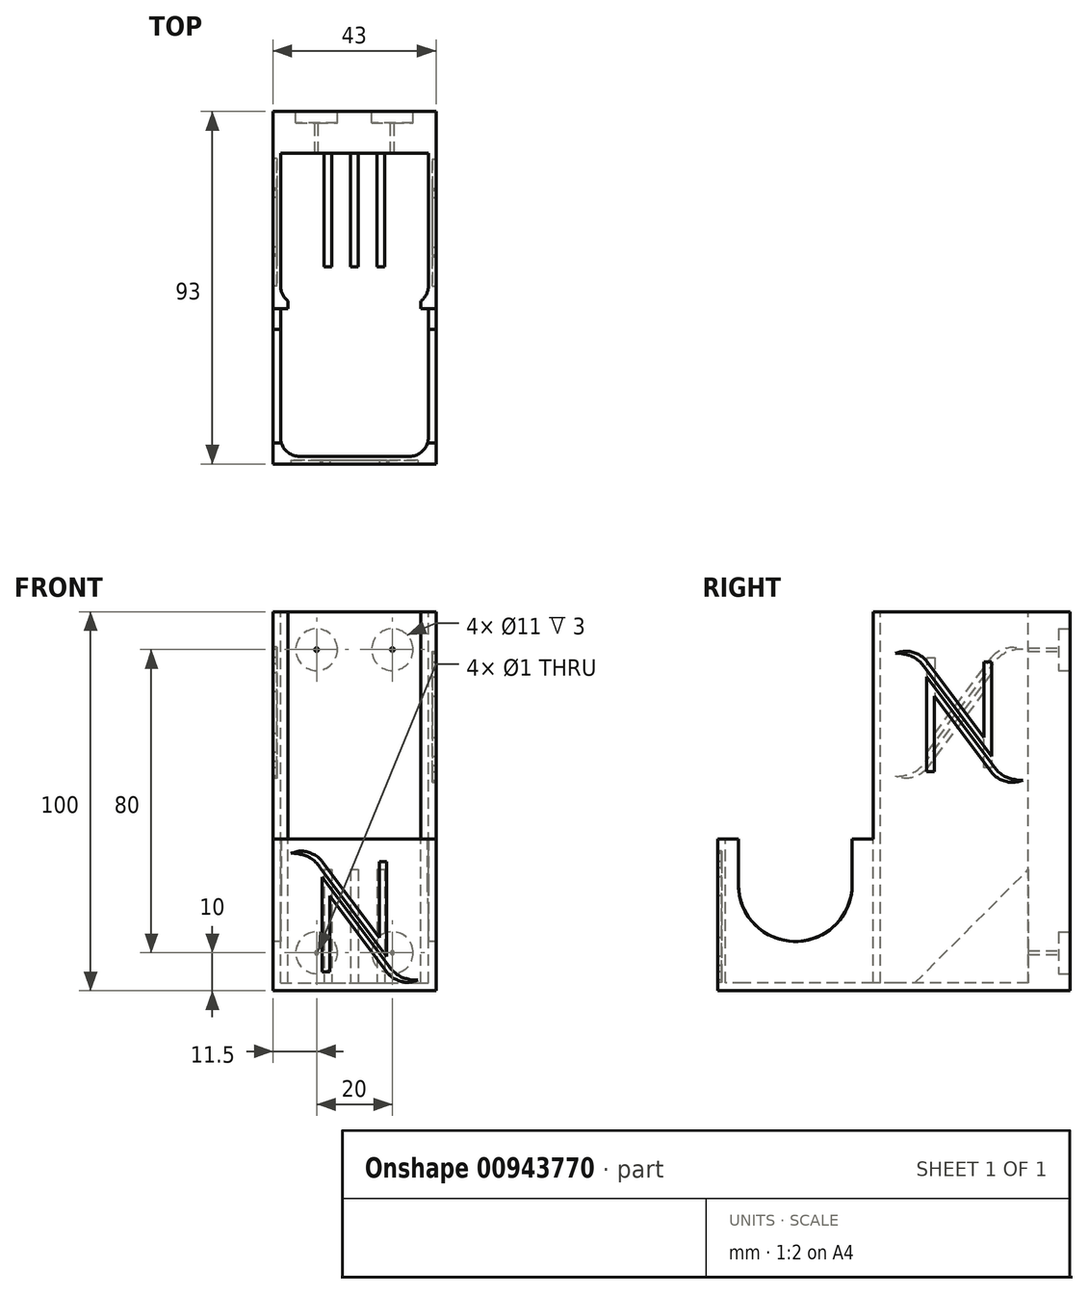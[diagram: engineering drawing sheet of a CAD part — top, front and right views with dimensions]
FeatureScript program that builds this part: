
annotation { "Feature Type Name" : "Feature", "Feature Type Description" : "" }
export const myFeature = defineFeature(function(context is Context, id is Id, definition is map)
    precondition{}
    {
        {
            var Q0;
            Q0=qCreatedBy(makeId("Top.planeOp"),FACE);
            var sketch = newSketch(context, id + "F0", { "sketchPlane" : qUnion([Q0])});
            skLineSegment(sketch, "E0.bottom", {"start": v(-21.5, 42) * mm, "end": v(21.5, 42) * mm});
            skLineSegment(sketch, "E0.top", {"start": v(-21.5, -42) * mm, "end": v(21.5, -42) * mm});
            skLineSegment(sketch, "E0.left", {"start": v(-21.5, 42) * mm, "end": v(-21.5, -42) * mm});
            skLineSegment(sketch, "E0.right", {"start": v(21.5, 42) * mm, "end": v(21.5, -42) * mm});
            skSolve(sketch);
        }
        {
            var Q0;
            Q0=makeQuery(id+"F0.imprint","IMPRINT",FACE,{"disambiguationData":[TD([[makeQuery(id+"F0.imprint","IMPRINT",EDGE,{"derivedFrom":sQuery(id+"F0.wireOp",EDGE,"E0.bottom")}),-1.0]])]});
            extrude(context, id + "F1", {"entities" : qUnion([Q0]), "depth" : 100 * mm, "offsetDistance" : 25 * mm});
        }
        {
            var Q0;
            Q0=makeQuery(id+"F1.opExtrude","CAP_FACE",FACE,{"disambiguationData":[OSD([sQuery(id+"F0.wireOp",EDGE,"E0.bottom"),sQuery(id+"F0.wireOp",EDGE,"E0.top"),sQuery(id+"F0.wireOp",EDGE,"E0.left"),sQuery(id+"F0.wireOp",EDGE,"E0.right")])],"isStart":false});
            var sketch = newSketch(context, id + "F2", { "sketchPlane" : qUnion([Q0])});
            skLineSegment(sketch, "E1.bottom", {"start": v(-21.5, -1) * mm, "end": v(21.5, -1) * mm});
            skLineSegment(sketch, "E1.top", {"start": v(-21.5, -42) * mm, "end": v(21.5, -42) * mm});
            skLineSegment(sketch, "E1.left", {"start": v(-21.5, -1) * mm, "end": v(-21.5, -42) * mm});
            skLineSegment(sketch, "E1.right", {"start": v(21.5, -1) * mm, "end": v(21.5, -42) * mm});
            skSolve(sketch);
        }
        {
            var Q0;
            Q0=makeQuery(id+"F2.imprint","IMPRINT",FACE,{"disambiguationData":[TD([[makeQuery(id+"F2.imprint","IMPRINT",EDGE,{"derivedFrom":sQuery(id+"F2.wireOp",EDGE,"E1.bottom")}),-1.0]])]});
            extrude(context, id + "F3", {"entities" : qUnion([Q0]), "operationType" : NewBodyOperationType.REMOVE, "oppositeDirection" : true, "depth" : 60 * mm, "offsetDistance" : 25 * mm});
        }
        {
            var Q0;
            Q0=makeQuery(id+"F3.boolean.opBoolean","COPY",FACE,{"derivedFrom":makeQuery(id+"F3.opExtrude","CAP_FACE",FACE,{"disambiguationData":[OSD([sQuery(id+"F2.wireOp",EDGE,"E1.bottom"),sQuery(id+"F2.wireOp",EDGE,"E1.top"),sQuery(id+"F2.wireOp",EDGE,"E1.left"),sQuery(id+"F2.wireOp",EDGE,"E1.right")])],"isStart":false})});
            var sketch = newSketch(context, id + "F4", { "sketchPlane" : qUnion([Q0])});
            skLineSegment(sketch, "E2.bottom", {"start": v(-19.5, -1) * mm, "end": v(19.5, -1) * mm});
            skLineSegment(sketch, "E2.top", {"start": v(-19.5, -40) * mm, "end": v(19.5, -40) * mm});
            skLineSegment(sketch, "E2.left", {"start": v(-19.5, -1) * mm, "end": v(-19.5, -40) * mm});
            skLineSegment(sketch, "E2.right", {"start": v(19.5, -1) * mm, "end": v(19.5, -40) * mm});
            skSolve(sketch);
        }
        {
            var Q0;
            Q0=makeQuery(id+"F4.imprint","IMPRINT",FACE,{"disambiguationData":[TD([[makeQuery(id+"F4.imprint","IMPRINT",EDGE,{"derivedFrom":sQuery(id+"F4.wireOp",EDGE,"E2.bottom")}),-1.0]])]});
            extrude(context, id + "F5", {"entities" : qUnion([Q0]), "operationType" : NewBodyOperationType.REMOVE, "oppositeDirection" : true, "depth" : 38 * mm, "offsetDistance" : 25 * mm});
        }
        {
            var Q0;
            Q0=makeQuery(id+"F1.opExtrude","CAP_FACE",FACE,{"disambiguationData":[OSD([sQuery(id+"F0.wireOp",EDGE,"E0.bottom"),sQuery(id+"F0.wireOp",EDGE,"E0.top"),sQuery(id+"F0.wireOp",EDGE,"E0.left"),sQuery(id+"F0.wireOp",EDGE,"E0.right")])],"isStart":false});
            var sketch = newSketch(context, id + "F6", { "sketchPlane" : qUnion([Q0])});
            skLineSegment(sketch, "E3.bottom", {"start": v(-19.5, 40) * mm, "end": v(19.5, 40) * mm});
            skLineSegment(sketch, "E3.top", {"start": v(-19.5, 1) * mm, "end": v(19.5, 1) * mm});
            skLineSegment(sketch, "E3.left", {"start": v(-19.5, 40) * mm, "end": v(-19.5, 1) * mm});
            skLineSegment(sketch, "E3.right", {"start": v(19.5, 40) * mm, "end": v(19.5, 1) * mm});
            skSolve(sketch);
        }
        {
            var Q0;
            Q0=makeQuery(id+"F6.imprint","IMPRINT",FACE,{"disambiguationData":[TD([[makeQuery(id+"F6.imprint","IMPRINT",EDGE,{"derivedFrom":sQuery(id+"F6.wireOp",EDGE,"E3.bottom")}),-1.0]])]});
            extrude(context, id + "F7", {"entities" : qUnion([Q0]), "operationType" : NewBodyOperationType.REMOVE, "oppositeDirection" : true, "depth" : 98 * mm, "offsetDistance" : 25 * mm});
        }
        {
            var Q0;
            Q0=makeQuery(id+"F1.opExtrude","CAP_FACE",FACE,{"disambiguationData":[OSD([sQuery(id+"F0.wireOp",EDGE,"E0.bottom"),sQuery(id+"F0.wireOp",EDGE,"E0.top"),sQuery(id+"F0.wireOp",EDGE,"E0.left"),sQuery(id+"F0.wireOp",EDGE,"E0.right")])],"isStart":false});
            var sketch = newSketch(context, id + "F8", { "sketchPlane" : qUnion([Q0])});
            skLineSegment(sketch, "E4.bottom", {"start": v(-17.5, 1) * mm, "end": v(17.5, 1) * mm});
            skLineSegment(sketch, "E4.top", {"start": v(-17.5, -1) * mm, "end": v(17.5, -1) * mm});
            skLineSegment(sketch, "E4.left", {"start": v(-17.5, 1) * mm, "end": v(-17.5, -1) * mm});
            skLineSegment(sketch, "E4.right", {"start": v(17.5, 1) * mm, "end": v(17.5, -1) * mm});
            skSolve(sketch);
        }
        {
            var Q0;
            Q0=makeQuery(id+"F8.imprint","IMPRINT",FACE,{"disambiguationData":[TD([[makeQuery(id+"F8.imprint","IMPRINT",EDGE,{"derivedFrom":sQuery(id+"F8.wireOp",EDGE,"E4.bottom")}),-1.0]])]});
            extrude(context, id + "F9", {"entities" : qUnion([Q0]), "operationType" : NewBodyOperationType.REMOVE, "oppositeDirection" : true, "depth" : 98 * mm, "offsetDistance" : 25 * mm});
        }
        {
            var Q0;
            Q0=makeQuery(id+"F7.boolean.opBoolean","COPY",EDGE,{"derivedFrom":makeQuery(id+"F7.opExtrude","SWEPT_EDGE",EDGE,{"disambiguationData":[OSD([sQuery(id+"F6.wireOp",EDGE,"E3.top"),sQuery(id+"F6.wireOp",EDGE,"E3.left")])]})});
            var Q1;
            Q1=makeQuery(id+"F7.boolean.opBoolean","COPY",EDGE,{"derivedFrom":makeQuery(id+"F7.opExtrude","SWEPT_EDGE",EDGE,{"disambiguationData":[OSD([sQuery(id+"F6.wireOp",EDGE,"E3.top"),sQuery(id+"F6.wireOp",EDGE,"E3.right")])]})});
            fillet(context, id + "F10", {"entities" : qUnion([Q0, Q1]), "radius" : 5 * mm, "tangentPropagation" : true, "allowEdgeOverflow" : false});
        }
        {
            var Q0;
            Q0=makeQuery(id+"F1.opExtrude","SWEPT_FACE",FACE,{"disambiguationData":[OSD([sQuery(id+"F0.wireOp",EDGE,"E0.left")])]});
            var sketch = newSketch(context, id + "F11", { "sketchPlane" : qUnion([Q0])});
            skArc(sketch, "E5", {"start": v(6.5, 28) * mm, "mid": v(21.5, 13) * mm, "end": v(36.5, 28) * mm});
            skLineSegment(sketch, "E6", {"start": v(6.5, 40) * mm, "end": v(6.5, 28) * mm});
            skLineSegment(sketch, "E7", {"start": v(36.5, 40) * mm, "end": v(36.5, 28) * mm});
            skLineSegment(sketch, "E8.0", {"start": v(6.5, 40) * mm, "end": v(36.5, 40) * mm});
            skPoint(sketch, "E9.orphan", {"position": v(1, 40) * mm});
            skPoint(sketch, "E10.orphan", {"position": v(42, 40) * mm});
            skSolve(sketch);
        }
        {
            var Q0;
            Q0=makeQuery(id+"F11.imprint","IMPRINT",FACE,{"disambiguationData":[TD([[makeQuery(id+"F11.imprint","IMPRINT",EDGE,{"derivedFrom":sQuery(id+"F11.wireOp",EDGE,"E5")}),1.0]])]});
            extrude(context, id + "F12", {"entities" : qUnion([Q0]), "operationType" : NewBodyOperationType.REMOVE, "oppositeDirection" : true, "depth" : 43 * mm, "offsetDistance" : 25 * mm});
        }
        {
            var Q0;
            Q0=makeQuery(id+"F5.boolean.opBoolean","COPY",EDGE,{"derivedFrom":makeQuery(id+"F5.opExtrude","SWEPT_EDGE",EDGE,{"disambiguationData":[OSD([sQuery(id+"F4.wireOp",EDGE,"E2.top"),sQuery(id+"F4.wireOp",EDGE,"E2.left")])]})});
            var Q1;
            Q1=makeQuery(id+"F5.boolean.opBoolean","COPY",EDGE,{"derivedFrom":makeQuery(id+"F5.opExtrude","SWEPT_EDGE",EDGE,{"disambiguationData":[OSD([sQuery(id+"F4.wireOp",EDGE,"E2.top"),sQuery(id+"F4.wireOp",EDGE,"E2.right")])]})});
            fillet(context, id + "F13", {"entities" : qUnion([Q0, Q1]), "radius" : 5 * mm, "tangentPropagation" : true, "allowEdgeOverflow" : false});
        }
        {
            var Q0;
            Q0=makeQuery(id+"F1.opExtrude","SWEPT_FACE",FACE,{"disambiguationData":[OSD([sQuery(id+"F0.wireOp",EDGE,"E0.bottom")])]});
            extrude(context, id + "F14", {"entities" : qUnion([Q0]), "operationType" : NewBodyOperationType.ADD, "depth" : 3 * mm, "offsetDistance" : 25 * mm});
        }
        {
            var Q0;
            Q0=makeQuery(id+"F14.opExtrude","CAP_FACE",FACE,{"disambiguationData":[OSD([sQuery(id+"F0.wireOp",EDGE,"E0.bottom")])],"isStart":false});
            var sketch = newSketch(context, id + "F15", { "sketchPlane" : qUnion([Q0])});
            skCircle(sketch, "E11", {"center": v(10, 90) * mm, "radius": 5.5 * mm});
            skCircle(sketch, "E12", {"center": v(-10, 90) * mm, "radius": 5.5 * mm});
            skCircle(sketch, "E13", {"center": v(-10, 10) * mm, "radius": 5.5 * mm});
            skCircle(sketch, "E14", {"center": v(10, 10) * mm, "radius": 5.5 * mm});
            skSolve(sketch);
        }
        {
            var Q0;
            Q0 = qSketchRegion(id + "F15", true);
            extrude(context, id + "F16", {"entities" : qUnion([Q0]), "operationType" : NewBodyOperationType.REMOVE, "oppositeDirection" : true, "depth" : 3 * mm, "offsetDistance" : 25 * mm});
        }
        {
            var Q0;
            Q0=makeQuery(id+"F9.boolean.opBoolean","MERGE",FACE,{"derivedFrom":[makeQuery(id+"F5.boolean.opBoolean","COPY",FACE,{"derivedFrom":makeQuery(id+"F5.opExtrude","CAP_FACE",FACE,{"disambiguationData":[OSD([sQuery(id+"F4.wireOp",EDGE,"E2.bottom"),sQuery(id+"F4.wireOp",EDGE,"E2.top"),sQuery(id+"F4.wireOp",EDGE,"E2.left"),sQuery(id+"F4.wireOp",EDGE,"E2.right")])],"isStart":false})}),makeQuery(id+"F7.boolean.opBoolean","COPY",FACE,{"derivedFrom":makeQuery(id+"F7.opExtrude","CAP_FACE",FACE,{"disambiguationData":[OSD([sQuery(id+"F6.wireOp",EDGE,"E3.bottom"),sQuery(id+"F6.wireOp",EDGE,"E3.top"),sQuery(id+"F6.wireOp",EDGE,"E3.left"),sQuery(id+"F6.wireOp",EDGE,"E3.right")])],"isStart":false})})],"fromTools":[makeQuery(id+"F9.opExtrude","CAP_FACE",FACE,{"disambiguationData":[OSD([sQuery(id+"F8.wireOp",EDGE,"E4.bottom"),sQuery(id+"F8.wireOp",EDGE,"E4.top"),sQuery(id+"F8.wireOp",EDGE,"E4.left"),sQuery(id+"F8.wireOp",EDGE,"E4.right")])],"isStart":false})]});
            var sketch = newSketch(context, id + "F17", { "sketchPlane" : qUnion([Q0])});
            skLineSegment(sketch, "E15.bottom", {"start": v(-1, 40) * mm, "end": v(1, 40) * mm});
            skLineSegment(sketch, "E15.top", {"start": v(-1, 10) * mm, "end": v(1, 10) * mm});
            skLineSegment(sketch, "E15.left", {"start": v(-1, 40) * mm, "end": v(-1, 10) * mm});
            skLineSegment(sketch, "E15.right", {"start": v(1, 40) * mm, "end": v(1, 10) * mm});
            skLineSegment(sketch, "E16.bottom", {"start": v(6, 40) * mm, "end": v(8, 40) * mm});
            skLineSegment(sketch, "E16.top", {"start": v(6, 10) * mm, "end": v(8, 10) * mm});
            skLineSegment(sketch, "E16.left", {"start": v(6, 40) * mm, "end": v(6, 10) * mm});
            skLineSegment(sketch, "E16.right", {"start": v(8, 40) * mm, "end": v(8, 10) * mm});
            skLineSegment(sketch, "E17.bottom", {"start": v(-8, 40) * mm, "end": v(-6, 40) * mm});
            skLineSegment(sketch, "E17.top", {"start": v(-8, 10) * mm, "end": v(-6, 10) * mm});
            skLineSegment(sketch, "E17.left", {"start": v(-8, 40) * mm, "end": v(-8, 10) * mm});
            skLineSegment(sketch, "E17.right", {"start": v(-6, 40) * mm, "end": v(-6, 10) * mm});
            skSolve(sketch);
        }
        {
            var Q0;
            Q0 = qSketchRegion(id + "F17", true);
            extrude(context, id + "F18", {"entities" : qUnion([Q0]), "operationType" : NewBodyOperationType.ADD, "depth" : 30 * mm, "offsetDistance" : 25 * mm});
        }
        {
            var Q0;
            Q0=makeQuery(id+"F18.opExtrude","CAP_EDGE",EDGE,{"disambiguationData":[OSD([sQuery(id+"F17.wireOp",EDGE,"E17.top")])],"isStart":false});
            var Q1;
            Q1=makeQuery(id+"F18.opExtrude","CAP_EDGE",EDGE,{"disambiguationData":[OSD([sQuery(id+"F17.wireOp",EDGE,"E15.top")])],"isStart":false});
            var Q2;
            Q2=makeQuery(id+"F18.opExtrude","CAP_EDGE",EDGE,{"disambiguationData":[OSD([sQuery(id+"F17.wireOp",EDGE,"E16.top")])],"isStart":false});
            chamfer(context, id + "F19", {"entities" : qUnion([Q0, Q1, Q2]), "width" : 30 * mm, "tangentPropagation" : true});
        }
        {
            var Q0;
            {var subQ0=sQuery(id+"F0.wireOp",EDGE,"E0.right");Q0=makeQuery(id+"F14.boolean.opBoolean","MERGE",FACE,{"derivedFrom":[makeQuery(id+"F1.opExtrude","SWEPT_FACE",FACE,{"disambiguationData":[OSD([subQ0])]}),makeQuery(id+"F14.opExtrude","SWEPT_FACE",FACE,{"disambiguationData":[OSD([sQuery(id+"F0.wireOp",EDGE,"E0.bottom"),subQ0])]})]});}
            var sketch = newSketch(context, id + "F20", { "sketchPlane" : qUnion([Q0])});
            skLineSegment(sketch, "E18", {"start": v(13.2, 82.76) * mm, "end": v(13.2, 57.76) * mm});
            skLineSegment(sketch, "E19", {"start": v(13.2, 57.76) * mm, "end": v(15.2, 57.76) * mm});
            skLineSegment(sketch, "E20", {"start": v(15.2, 57.76) * mm, "end": v(15.2, 77.76) * mm});
            skLineSegment(sketch, "E21", {"start": v(15.2, 77.76) * mm, "end": v(30.2, 57.76) * mm});
            skFitSpline(sketch, "E22", {"points": [v(30.2, 57.76) * mm, v(31.52, 56.4) * mm, v(33.7, 55.35) * mm, v(35.88, 54.97) * mm, v(38.53, 55.54) * mm], "startDerivative": vector(5.12, -6.4) * mm, "endDerivative": vector(10.04, 2.97) * mm});
            skLineSegment(sketch, "E23", {"start": v(13.2, 82.76) * mm, "end": v(30.71, 59.42) * mm});
            skFitSpline(sketch, "E24", {"points": [v(38.53, 55.54) * mm, v(37.43, 55.54) * mm, v(35.83, 55.83) * mm, v(34.45, 56.22) * mm, v(33.06, 57) * mm, v(31.64, 58.2) * mm, v(30.71, 59.42) * mm], "startDerivative": vector(-7.36, -0.38) * mm, "endDerivative": vector(-4.99, 7.42) * mm});
            skLineSegment(sketch, "E25", {"start": v(30.26, 61.8) * mm, "end": v(30.26, 86.8) * mm});
            skLineSegment(sketch, "E26", {"start": v(30.26, 86.8) * mm, "end": v(28.26, 86.8) * mm});
            skLineSegment(sketch, "E27", {"start": v(28.26, 86.8) * mm, "end": v(28.26, 66.8) * mm});
            skLineSegment(sketch, "E28", {"start": v(28.26, 66.8) * mm, "end": v(13.26, 86.8) * mm});
            skFitSpline(sketch, "E29", {"points": [v(13.26, 86.8) * mm, v(11.94, 88.17) * mm, v(9.76, 89.22) * mm, v(7.58, 89.6) * mm, v(4.93, 89.03) * mm], "startDerivative": vector(-5.12, 6.4) * mm, "endDerivative": vector(-10.04, -2.97) * mm});
            skLineSegment(sketch, "E30", {"start": v(30.26, 61.8) * mm, "end": v(12.75, 85.15) * mm});
            skFitSpline(sketch, "E31", {"points": [v(4.93, 89.03) * mm, v(6.03, 89.03) * mm, v(7.63, 88.74) * mm, v(9.01, 88.35) * mm, v(10.4, 87.56) * mm, v(11.82, 86.38) * mm, v(12.75, 85.15) * mm], "startDerivative": vector(7.36, 0.38) * mm, "endDerivative": vector(4.99, -7.42) * mm});
            skSolve(sketch);
        }
        {
            var Q0;
            Q0 = qSketchRegion(id + "F20", true);
            extrude(context, id + "F21", {"entities" : qUnion([Q0]), "operationType" : NewBodyOperationType.REMOVE, "oppositeDirection" : true, "depth" : 1 * mm, "offsetDistance" : 25 * mm});
        }
        {
            var Q0;
            {var subQ0=sQuery(id+"F0.wireOp",EDGE,"E0.left");Q0=makeQuery(id+"F14.boolean.opBoolean","MERGE",FACE,{"derivedFrom":[makeQuery(id+"F1.opExtrude","SWEPT_FACE",FACE,{"disambiguationData":[OSD([subQ0])]}),makeQuery(id+"F14.opExtrude","SWEPT_FACE",FACE,{"disambiguationData":[OSD([sQuery(id+"F0.wireOp",EDGE,"E0.bottom"),subQ0])]})]});}
            var sketch = newSketch(context, id + "F22", { "sketchPlane" : qUnion([Q0])});
            skLineSegment(sketch, "E32", {"start": v(-30.3, 83.83) * mm, "end": v(-30.3, 58.83) * mm});
            skLineSegment(sketch, "E33", {"start": v(-30.3, 58.83) * mm, "end": v(-28.3, 58.83) * mm});
            skLineSegment(sketch, "E34", {"start": v(-28.3, 58.83) * mm, "end": v(-28.3, 78.83) * mm});
            skLineSegment(sketch, "E35", {"start": v(-28.3, 78.83) * mm, "end": v(-13.3, 58.83) * mm});
            skFitSpline(sketch, "E36", {"points": [v(-13.3, 58.83) * mm, v(-11.99, 57.46) * mm, v(-9.8, 56.42) * mm, v(-7.63, 56.04) * mm, v(-4.97, 56.6) * mm], "startDerivative": vector(5.12, -6.4) * mm, "endDerivative": vector(10.04, 2.97) * mm});
            skLineSegment(sketch, "E37", {"start": v(-30.3, 83.83) * mm, "end": v(-12.8, 60.48) * mm});
            skFitSpline(sketch, "E38", {"points": [v(-4.97, 56.6) * mm, v(-6.08, 56.6) * mm, v(-7.68, 56.9) * mm, v(-9.06, 57.29) * mm, v(-10.45, 58.08) * mm, v(-11.87, 59.26) * mm, v(-12.8, 60.48) * mm], "startDerivative": vector(-7.36, -0.38) * mm, "endDerivative": vector(-4.99, 7.42) * mm});
            skLineSegment(sketch, "E39", {"start": v(-13.25, 62.88) * mm, "end": v(-13.25, 87.88) * mm});
            skLineSegment(sketch, "E40", {"start": v(-13.25, 87.88) * mm, "end": v(-15.25, 87.88) * mm});
            skLineSegment(sketch, "E41", {"start": v(-15.25, 87.88) * mm, "end": v(-15.25, 67.88) * mm});
            skLineSegment(sketch, "E42", {"start": v(-15.25, 67.88) * mm, "end": v(-30.25, 87.88) * mm});
            skFitSpline(sketch, "E43", {"points": [v(-30.25, 87.88) * mm, v(-31.56, 89.24) * mm, v(-33.74, 90.28) * mm, v(-35.92, 90.66) * mm, v(-38.58, 90.1) * mm], "startDerivative": vector(-5.12, 6.4) * mm, "endDerivative": vector(-10.04, -2.97) * mm});
            skLineSegment(sketch, "E44", {"start": v(-13.25, 62.88) * mm, "end": v(-30.76, 86.22) * mm});
            skFitSpline(sketch, "E45", {"points": [v(-38.58, 90.1) * mm, v(-37.47, 90.1) * mm, v(-35.87, 89.81) * mm, v(-34.5, 89.42) * mm, v(-33.1, 88.63) * mm, v(-31.68, 87.44) * mm, v(-30.76, 86.22) * mm], "startDerivative": vector(7.36, 0.38) * mm, "endDerivative": vector(4.99, -7.42) * mm});
            skSolve(sketch);
        }
        {
            var Q0;
            Q0 = qSketchRegion(id + "F22", true);
            extrude(context, id + "F23", {"entities" : qUnion([Q0]), "operationType" : NewBodyOperationType.REMOVE, "oppositeDirection" : true, "depth" : 1 * mm, "offsetDistance" : 25 * mm});
        }
        {
            var Q0;
            Q0=makeQuery(id+"F1.opExtrude","SWEPT_FACE",FACE,{"disambiguationData":[OSD([sQuery(id+"F0.wireOp",EDGE,"E0.top")])]});
            var sketch = newSketch(context, id + "F24", { "sketchPlane" : qUnion([Q0])});
            skLineSegment(sketch, "E46", {"start": v(-8.54, 30) * mm, "end": v(-8.54, 5) * mm});
            skLineSegment(sketch, "E47", {"start": v(-8.54, 5) * mm, "end": v(-6.54, 5) * mm});
            skLineSegment(sketch, "E48", {"start": v(-6.54, 5) * mm, "end": v(-6.54, 25) * mm});
            skLineSegment(sketch, "E49", {"start": v(-6.54, 25) * mm, "end": v(8.46, 5) * mm});
            skFitSpline(sketch, "E50", {"points": [v(8.46, 5) * mm, v(9.78, 3.63) * mm, v(11.96, 2.6) * mm, v(14.14, 2.21) * mm, v(16.8, 2.78) * mm], "startDerivative": vector(5.12, -6.4) * mm, "endDerivative": vector(10.04, 2.97) * mm});
            skLineSegment(sketch, "E51", {"start": v(-8.54, 30) * mm, "end": v(8.97, 6.65) * mm});
            skFitSpline(sketch, "E52", {"points": [v(16.8, 2.78) * mm, v(15.69, 2.78) * mm, v(14.09, 3.06) * mm, v(12.7, 3.46) * mm, v(11.32, 4.25) * mm, v(9.9, 5.43) * mm, v(8.97, 6.65) * mm], "startDerivative": vector(-7.36, -0.38) * mm, "endDerivative": vector(-4.99, 7.42) * mm});
            skLineSegment(sketch, "E53", {"start": v(8.52, 9.05) * mm, "end": v(8.52, 34.05) * mm});
            skLineSegment(sketch, "E54", {"start": v(8.52, 34.05) * mm, "end": v(6.52, 34.05) * mm});
            skLineSegment(sketch, "E55", {"start": v(6.52, 34.05) * mm, "end": v(6.52, 14.05) * mm});
            skLineSegment(sketch, "E56", {"start": v(6.52, 14.05) * mm, "end": v(-8.48, 34.05) * mm});
            skFitSpline(sketch, "E57", {"points": [v(-8.48, 34.05) * mm, v(-9.8, 35.41) * mm, v(-11.98, 36.46) * mm, v(-14.16, 36.84) * mm, v(-16.81, 36.27) * mm], "startDerivative": vector(-5.12, 6.4) * mm, "endDerivative": vector(-10.04, -2.97) * mm});
            skLineSegment(sketch, "E58", {"start": v(8.52, 9.05) * mm, "end": v(-9, 32.4) * mm});
            skFitSpline(sketch, "E59", {"points": [v(-16.81, 36.27) * mm, v(-15.7, 36.27) * mm, v(-14.1, 35.98) * mm, v(-12.73, 35.59) * mm, v(-11.34, 34.8) * mm, v(-9.92, 33.62) * mm, v(-9, 32.4) * mm], "startDerivative": vector(7.36, 0.38) * mm, "endDerivative": vector(4.99, -7.42) * mm});
            skSolve(sketch);
        }
        {
            var Q0;
            Q0 = qSketchRegion(id + "F24", true);
            extrude(context, id + "F25", {"entities" : qUnion([Q0]), "operationType" : NewBodyOperationType.REMOVE, "oppositeDirection" : true, "depth" : 1 * mm, "offsetDistance" : 25 * mm});
        }
        {
            var Q0;
            Q0=makeQuery(id+"F16.boolean.opBoolean","COPY",FACE,{"derivedFrom":makeQuery(id+"F16.opExtrude","CAP_FACE",FACE,{"disambiguationData":[OSD([sQuery(id+"F15.wireOp",EDGE,"E12")])],"isStart":false})});
            var sketch = newSketch(context, id + "F26", { "sketchPlane" : qUnion([Q0])});
            skCircle(sketch, "E60", {"center": v(-10, 90) * mm, "radius": 0.5 * mm});
            skSolve(sketch);
        }
        {
            var Q0;
            Q0 = qSketchRegion(id + "F26", true);
            extrude(context, id + "F27", {"entities" : qUnion([Q0]), "operationType" : NewBodyOperationType.REMOVE, "oppositeDirection" : true, "depth" : 2 * mm, "offsetDistance" : 25 * mm});
        }
        {
            var Q0;
            Q0=makeQuery(id+"F16.boolean.opBoolean","COPY",FACE,{"derivedFrom":makeQuery(id+"F16.opExtrude","CAP_FACE",FACE,{"disambiguationData":[OSD([sQuery(id+"F15.wireOp",EDGE,"E11")])],"isStart":false})});
            var sketch = newSketch(context, id + "F28", { "sketchPlane" : qUnion([Q0])});
            skCircle(sketch, "E61", {"center": v(10, 90) * mm, "radius": 0.5 * mm});
            skSolve(sketch);
        }
        {
            var Q0;
            Q0 = qSketchRegion(id + "F28", true);
            extrude(context, id + "F29", {"entities" : qUnion([Q0]), "operationType" : NewBodyOperationType.REMOVE, "oppositeDirection" : true, "depth" : 2 * mm, "offsetDistance" : 25 * mm});
        }
        {
            var Q0;
            Q0=makeQuery(id+"F14.opExtrude","CAP_FACE",FACE,{"disambiguationData":[OSD([sQuery(id+"F0.wireOp",EDGE,"E0.bottom")])],"isStart":false});
            extrude(context, id + "F30", {"entities" : qUnion([Q0]), "operationType" : NewBodyOperationType.ADD, "depth" : 6 * mm, "offsetDistance" : 25 * mm});
        }
        {
            var Q0;
            Q0=makeQuery(id+"F16.boolean.opBoolean","COPY",FACE,{"derivedFrom":makeQuery(id+"F16.opExtrude","CAP_FACE",FACE,{"disambiguationData":[OSD([sQuery(id+"F15.wireOp",EDGE,"E12")])],"isStart":false})});
            extrude(context, id + "F31", {"entities" : qUnion([Q0]), "operationType" : NewBodyOperationType.ADD, "depth" : 6 * mm, "offsetDistance" : 25 * mm});
        }
        {
            var Q0;
            Q0=makeQuery(id+"F16.boolean.opBoolean","COPY",FACE,{"derivedFrom":makeQuery(id+"F16.opExtrude","CAP_FACE",FACE,{"disambiguationData":[OSD([sQuery(id+"F15.wireOp",EDGE,"E11")])],"isStart":false})});
            extrude(context, id + "F32", {"entities" : qUnion([Q0]), "operationType" : NewBodyOperationType.ADD, "depth" : 6 * mm, "offsetDistance" : 25 * mm});
        }
        {
            var Q0;
            Q0=makeQuery(id+"F16.boolean.opBoolean","COPY",FACE,{"derivedFrom":makeQuery(id+"F16.opExtrude","CAP_FACE",FACE,{"disambiguationData":[OSD([sQuery(id+"F15.wireOp",EDGE,"E13")])],"isStart":false})});
            var sketch = newSketch(context, id + "F33", { "sketchPlane" : qUnion([Q0])});
            skCircle(sketch, "E62", {"center": v(-10, 10) * mm, "radius": 0.5 * mm});
            skSolve(sketch);
        }
        {
            var Q0;
            Q0 = qSketchRegion(id + "F33", true);
            extrude(context, id + "F34", {"entities" : qUnion([Q0]), "operationType" : NewBodyOperationType.REMOVE, "oppositeDirection" : true, "depth" : 2 * mm, "offsetDistance" : 25 * mm});
        }
        {
            var Q0;
            Q0=makeQuery(id+"F16.boolean.opBoolean","COPY",FACE,{"derivedFrom":makeQuery(id+"F16.opExtrude","CAP_FACE",FACE,{"disambiguationData":[OSD([sQuery(id+"F15.wireOp",EDGE,"E14")])],"isStart":false})});
            var sketch = newSketch(context, id + "F35", { "sketchPlane" : qUnion([Q0])});
            skCircle(sketch, "E63", {"center": v(10, 10) * mm, "radius": 0.5 * mm});
            skSolve(sketch);
        }
        {
            var Q0;
            Q0 = qSketchRegion(id + "F35", true);
            extrude(context, id + "F36", {"entities" : qUnion([Q0]), "operationType" : NewBodyOperationType.REMOVE, "oppositeDirection" : true, "depth" : 2 * mm, "offsetDistance" : 25 * mm});
        }
        {
            var Q0;
            Q0=makeQuery(id+"F16.boolean.opBoolean","COPY",FACE,{"derivedFrom":makeQuery(id+"F16.opExtrude","CAP_FACE",FACE,{"disambiguationData":[OSD([sQuery(id+"F15.wireOp",EDGE,"E13")])],"isStart":false})});
            extrude(context, id + "F37", {"entities" : qUnion([Q0]), "operationType" : NewBodyOperationType.ADD, "depth" : 6 * mm, "offsetDistance" : 25 * mm});
        }
        {
            var Q0;
            Q0=makeQuery(id+"F16.boolean.opBoolean","COPY",FACE,{"derivedFrom":makeQuery(id+"F16.opExtrude","CAP_FACE",FACE,{"disambiguationData":[OSD([sQuery(id+"F15.wireOp",EDGE,"E14")])],"isStart":false})});
            extrude(context, id + "F38", {"entities" : qUnion([Q0]), "operationType" : NewBodyOperationType.ADD, "depth" : 6 * mm, "offsetDistance" : 25 * mm});
        }
    });
